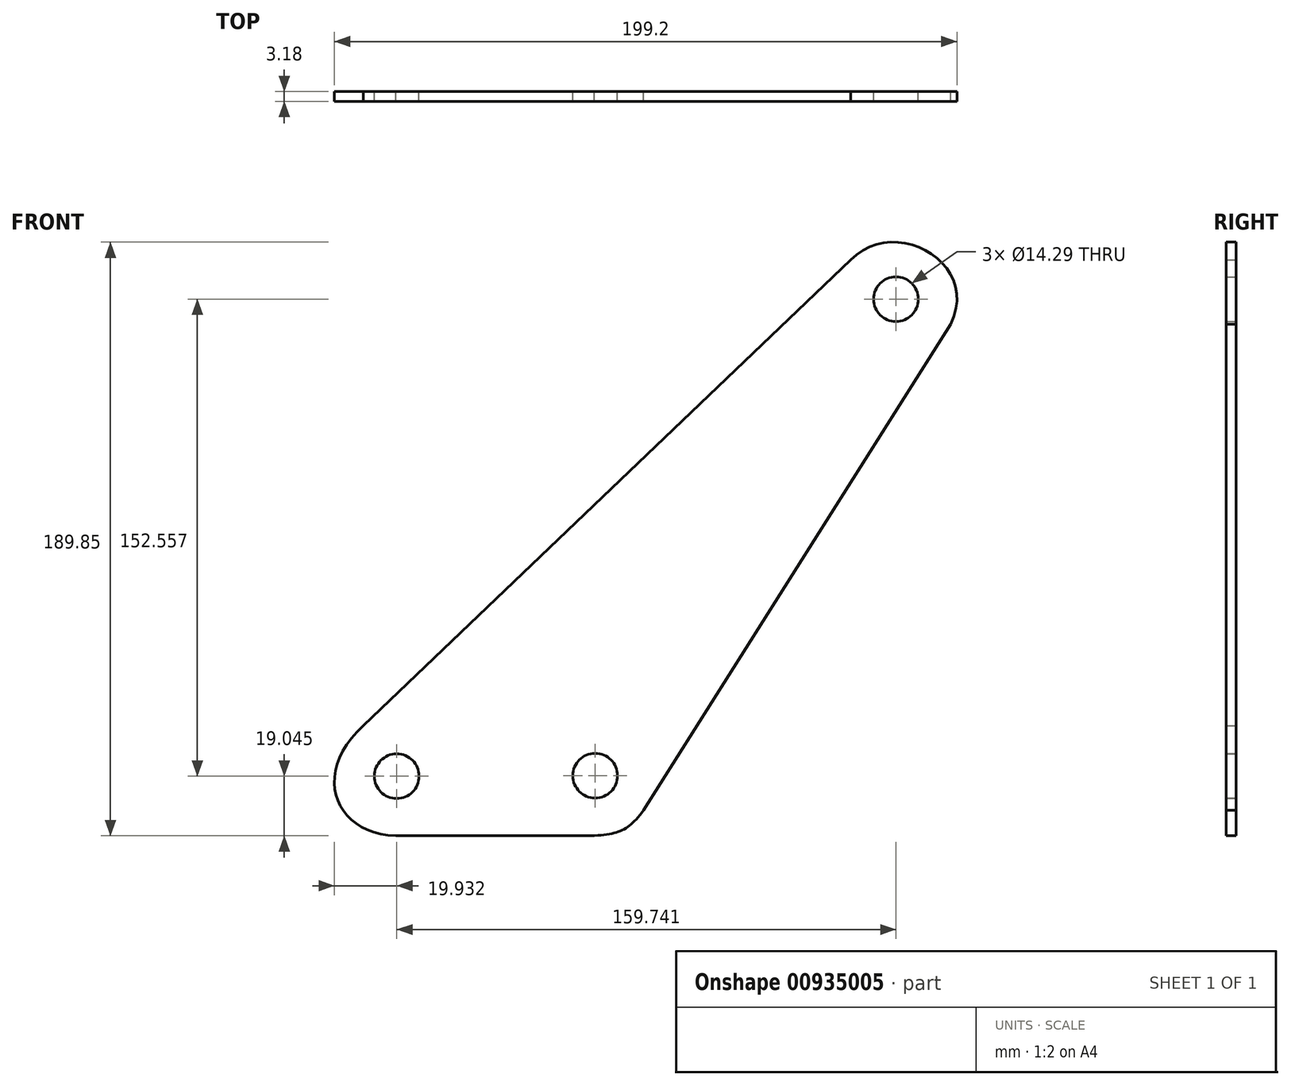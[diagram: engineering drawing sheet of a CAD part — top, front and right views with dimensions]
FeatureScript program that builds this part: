
annotation { "Feature Type Name" : "Feature", "Feature Type Description" : "" }
export const myFeature = defineFeature(function(context is Context, id is Id, definition is map)
    precondition{}
    {
        {
            var Q0;
            Q0=qCreatedBy(makeId("Front.planeOp"),FACE);
            var sketch = newSketch(context, id + "F0", { "sketchPlane" : qUnion([Q0])});
            skCircle(sketch, "E0", {"center": v(65.42, 172.98) * mm, "radius": 7.14 * mm});
            skCircle(sketch, "E1", {"center": v(-94.32, 20.43) * mm, "radius": 7.14 * mm});
            skCircle(sketch, "E2", {"center": v(-30.82, 20.58) * mm, "radius": 7.14 * mm});
            skLineSegment(sketch, "E3", {"start": v(50.95, 185.5) * mm, "end": v(-105.01, 36.55) * mm});
            skLineSegment(sketch, "E4", {"start": v(-94.62, 1.38) * mm, "end": v(-31.05, 1.38) * mm});
            skLineSegment(sketch, "E5", {"start": v(82.93, 165.02) * mm, "end": v(-15.3, 9.48) * mm});
            skFitSpline(sketch, "E6", {"points": [v(-105.01, 36.55) * mm, v(-94.62, 1.38) * mm], "startDerivative": vector(-49.93, -45.31) * mm, "endDerivative": vector(59.27, -1.97) * mm});
            skFitSpline(sketch, "E7", {"points": [v(-31.05, 1.38) * mm, v(-15.3, 9.48) * mm], "startDerivative": vector(25.22, 1.97) * mm, "endDerivative": vector(14.76, 18.71) * mm});
            skFitSpline(sketch, "E8", {"points": [v(82.93, 165.02) * mm, v(50.95, 185.5) * mm], "startDerivative": vector(29.12, 58.53) * mm, "endDerivative": vector(-42.06, -43.7) * mm});
            skSolve(sketch);
        }
        {
            var Q0;
            Q0 = qSketchRegion(id + "F0", true);
            extrude(context, id + "F1", {"entities" : qUnion([Q0]), "depth" : 3.17 * mm, "offsetDistance" : 25.4 * mm});
        }
    });
